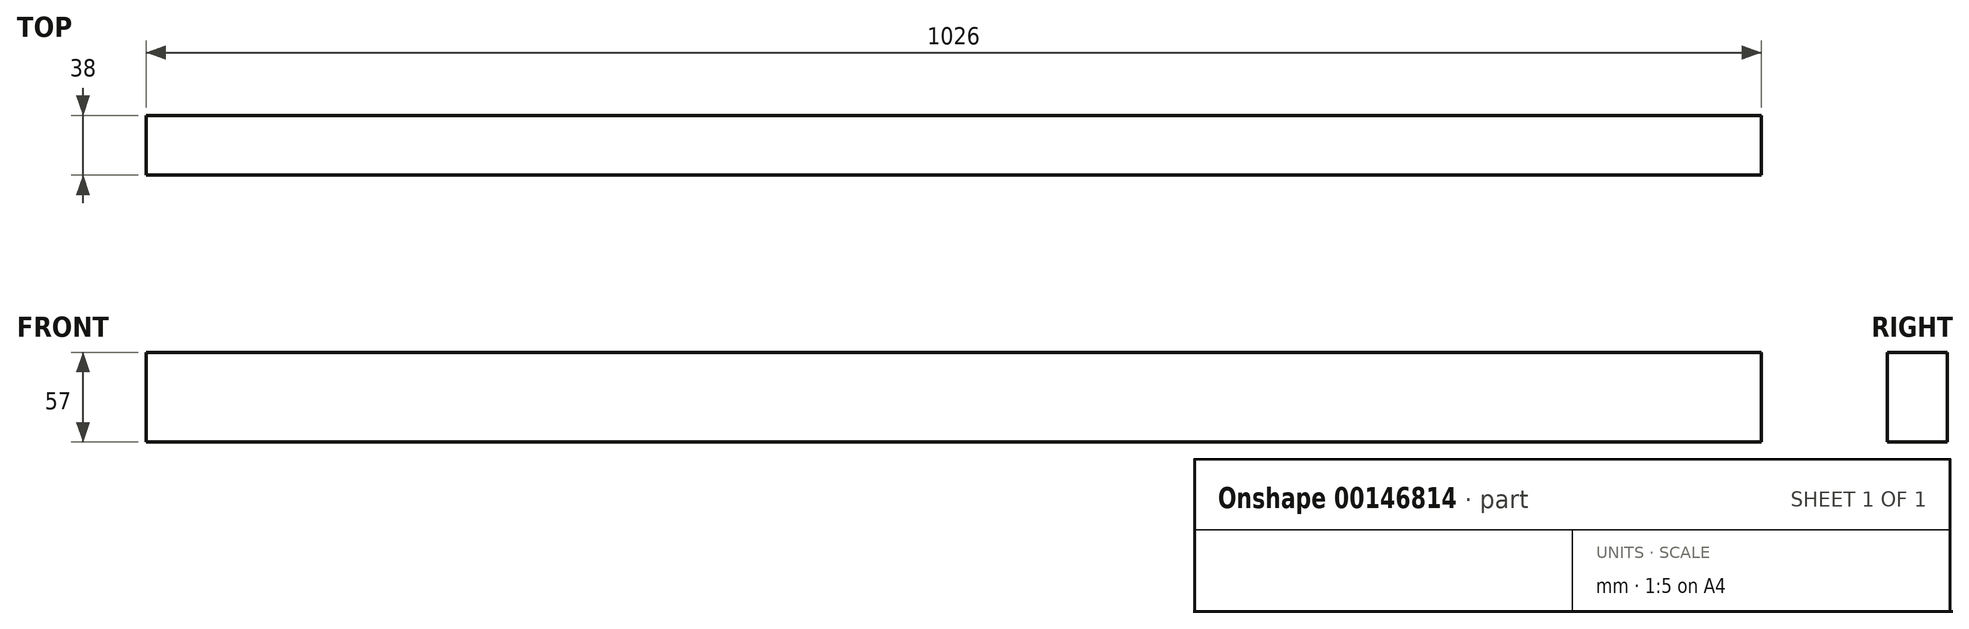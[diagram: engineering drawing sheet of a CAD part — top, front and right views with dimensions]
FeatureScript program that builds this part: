
annotation { "Feature Type Name" : "Feature", "Feature Type Description" : "" }
export const myFeature = defineFeature(function(context is Context, id is Id, definition is map)
    precondition{}
    {
        {
            var Q0;
            Q0=qCreatedBy(makeId("Top.planeOp"),FACE);
            var sketch = newSketch(context, id + "F0", { "sketchPlane" : qUnion([Q0])});
            skLineSegment(sketch, "E0.bottom", {"start": v(0, 0) * mm, "end": v(1026, 0) * mm});
            skLineSegment(sketch, "E0.top", {"start": v(0, 38) * mm, "end": v(1026, 38) * mm});
            skLineSegment(sketch, "E0.left", {"start": v(0, 0) * mm, "end": v(0, 38) * mm});
            skLineSegment(sketch, "E0.right", {"start": v(1026, 0) * mm, "end": v(1026, 38) * mm});
            skSolve(sketch);
        }
        {
            var Q0;
            Q0=qSketchRegion(id+"F0",true);
            extrude(context, id + "F1", {"entities" : qUnion([Q0]), "depth" : 57 * mm});
        }
    });
